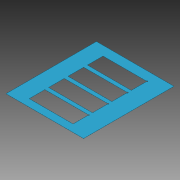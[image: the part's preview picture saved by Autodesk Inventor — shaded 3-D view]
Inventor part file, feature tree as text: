
AUTODESK INVENTOR PART (.ipt)
format: ipt  version: 2013 (Build 170138000, 138)  size: 112,128 bytes
history: native  units: mm
features: extrude x2, sketch x2, reference x2, plane x1, pattern_linear x1
ambient origin geometry x8: Origin, YZ Plane, XZ Plane, XY Plane, X Axis, Y Axis, Z Axis, Center Point
bodies: Volumenkörper1 (feature_tree)
feature tree (8):
  plane  "Arbeitsebene1"
  extrude  "Extrusion1"  Depth=3.0mm
  extrude  "Extrusion2"  Depth=2.0mm
  pattern_linear  "Rechteckige Anordnung1"  Spacing1=0.1mm  [1 undecoded]
  sketch  "Skizze2"  dims[d3=0.1mm d4=0.0mm d5=3.0mm]
  reference  "Referenz2"
  sketch  "Skizze3"  dims[d6=3.0mm d7=2.0mm d8=0.1mm d9=0.0mm d10=40.0mm d12=30.0mm]
  reference  "Referenz3"
note: 1 required parameter value undecoded (feature->parameter linkage not recoverable at this tier; creation-order binding heuristic only, values carry confidence <= 0.55)
